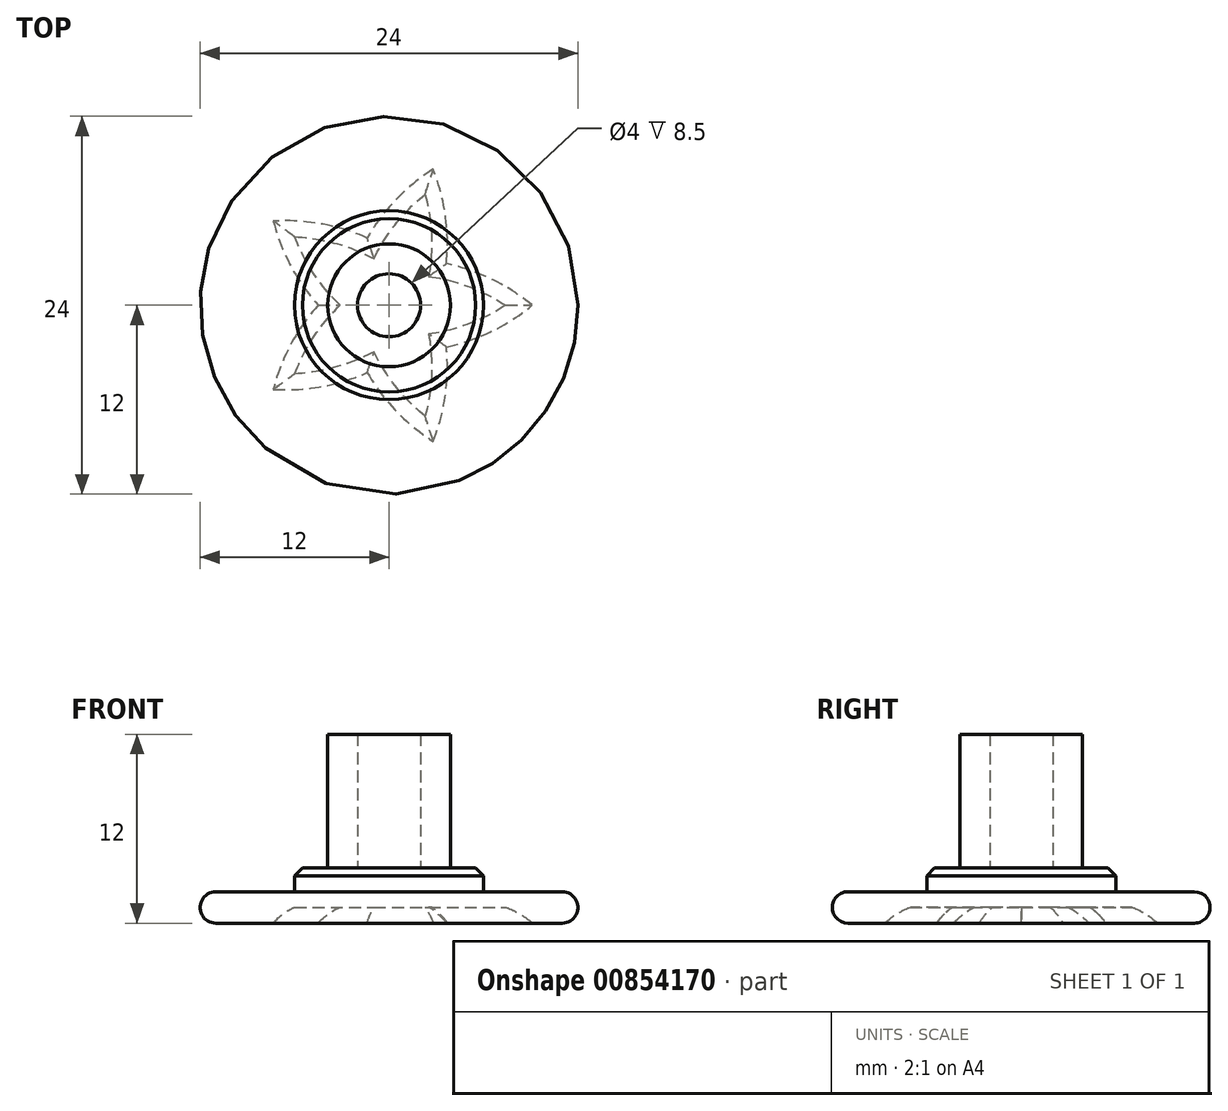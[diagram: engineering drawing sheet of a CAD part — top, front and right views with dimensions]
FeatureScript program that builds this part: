
annotation { "Feature Type Name" : "Feature", "Feature Type Description" : "" }
export const myFeature = defineFeature(function(context is Context, id is Id, definition is map)
    precondition{}
    {
        {
            var Q0;
            Q0=qCreatedBy(makeId("Top.planeOp"),FACE);
            var sketch = newSketch(context, id + "F0", { "sketchPlane" : qUnion([Q0])});
            skCircle(sketch, "E0", {"center": v(0, 0) * mm, "radius": 3.9 * mm});
            skCircle(sketch, "E1", {"center": v(0, 0) * mm, "radius": 2 * mm});
            skCircle(sketch, "E2", {"center": v(0, 0) * mm, "radius": 12 * mm});
            skCircle(sketch, "E3", {"center": v(0, 0) * mm, "radius": 6 * mm});
            skCircle(sketch, "E4.cCircle", {"center": v(0, 0) * mm, "radius": 2.5 * mm, "construction": true});
            skLineSegment(sketch, "E4.0", {"start": v(-2.5, -1.82) * mm, "end": v(-2.5, 1.82) * mm});
            skLineSegment(sketch, "E4.1", {"start": v(-2.5, 1.82) * mm, "end": v(0.95, 2.94) * mm});
            skLineSegment(sketch, "E4.2", {"start": v(0.95, 2.94) * mm, "end": v(3.1, 0) * mm});
            skLineSegment(sketch, "E4.3", {"start": v(3.1, 0) * mm, "end": v(0.95, -2.94) * mm});
            skLineSegment(sketch, "E4.4", {"start": v(0.95, -2.94) * mm, "end": v(-2.5, -1.82) * mm});
            skPoint(sketch, "E4.0.midPoint", {"position": v(-2.5, 0) * mm});
            skLineSegment(sketch, "E5", {"start": v(-2.5, 0) * mm, "end": v(-4.5, 0) * mm});
            skLineSegment(sketch, "E6", {"start": v(-0.77, -2.38) * mm, "end": v(-1.4, -4.28) * mm});
            skLineSegment(sketch, "E7", {"start": v(2.02, -1.47) * mm, "end": v(3.64, -2.65) * mm});
            skLineSegment(sketch, "E8", {"start": v(2.02, 1.47) * mm, "end": v(3.64, 2.65) * mm});
            skLineSegment(sketch, "E9", {"start": v(-0.77, 2.38) * mm, "end": v(-1.4, 4.28) * mm});
            skLineSegment(sketch, "E10", {"start": v(3.1, 0) * mm, "end": v(9.1, 0) * mm});
            skLineSegment(sketch, "E11", {"start": v(0.95, -2.94) * mm, "end": v(2.8, -8.65) * mm});
            skLineSegment(sketch, "E12", {"start": v(-2.5, -1.82) * mm, "end": v(-7.35, -5.34) * mm});
            skLineSegment(sketch, "E13", {"start": v(-2.5, 1.82) * mm, "end": v(-7.35, 5.34) * mm});
            skLineSegment(sketch, "E14", {"start": v(0.95, 2.94) * mm, "end": v(2.8, 8.65) * mm});
            skArc(sketch, "E15", {"start": v(0.95, 2.94) * mm, "mid": v(-3, 4.86) * mm, "end": v(-7.35, 5.34) * mm});
            skArc(sketch, "E16", {"start": v(2.8, 8.65) * mm, "mid": v(-0.44, 5.7) * mm, "end": v(-2.5, 1.82) * mm});
            skArc(sketch, "E17", {"start": v(3.1, 0) * mm, "mid": v(3.7, 4.35) * mm, "end": v(2.8, 8.65) * mm});
            skArc(sketch, "E18", {"start": v(9.1, 0) * mm, "mid": v(5.28, 2.17) * mm, "end": v(0.95, 2.94) * mm});
            skArc(sketch, "E19", {"start": v(0.95, -2.94) * mm, "mid": v(5.28, -2.17) * mm, "end": v(9.1, 0) * mm});
            skArc(sketch, "E20", {"start": v(2.8, -8.65) * mm, "mid": v(3.7, -4.35) * mm, "end": v(3.1, 0) * mm});
            skArc(sketch, "E21", {"start": v(-2.5, -1.82) * mm, "mid": v(-0.44, -5.7) * mm, "end": v(2.8, -8.65) * mm});
            skArc(sketch, "E22", {"start": v(-7.35, -5.34) * mm, "mid": v(-3, -4.86) * mm, "end": v(0.95, -2.94) * mm});
            skArc(sketch, "E23", {"start": v(-2.5, 1.82) * mm, "mid": v(-5.55, -1.34) * mm, "end": v(-7.35, -5.34) * mm});
            skArc(sketch, "E24", {"start": v(-7.35, 5.34) * mm, "mid": v(-5.55, 1.34) * mm, "end": v(-2.5, -1.82) * mm});
            skSolve(sketch);
        }
        {
            var Q0;
            Q0=makeQuery(id+"F0.imprint","IMPRINT",FACE,{"disambiguationData":[TD([[makeQuery(id+"F0.imprint","IMPRINT",EDGE,{"derivedFrom":sQuery(id+"F0.wireOp",EDGE,"E2")}),1.0]])]});
            extrude(context, id + "F1", {"entities" : qUnion([Q0]), "depth" : 2 * mm, "offsetDistance" : 25 * mm});
        }
        {
            var Q0;
            {var subQ0=sQuery(id+"F0.wireOp",EDGE,"E15");var subQ1=sQuery(id+"F0.wireOp",EDGE,"E3");var subQ2=makeQuery(id+"F0.imprint","INTERSECT",VERTEX,{"derivedFrom":[subQ1,subQ0]});Q0=makeQuery(id+"F0.imprint","IMPRINT",FACE,{"disambiguationData":[TD([[makeQuery(id+"F0.imprint","IMPRINT",EDGE,{"disambiguationData":[TD([[subQ2,-1.0]])],"derivedFrom":subQ1}),-1.0]])]});}
            var Q1;
            {var subQ0=sQuery(id+"F0.wireOp",EDGE,"E13");var subQ1=sQuery(id+"F0.wireOp",EDGE,"E3");var subQ2=makeQuery(id+"F0.imprint","INTERSECT",VERTEX,{"derivedFrom":[subQ1,subQ0]});Q1=makeQuery(id+"F0.imprint","IMPRINT",FACE,{"disambiguationData":[TD([[makeQuery(id+"F0.imprint","IMPRINT",EDGE,{"disambiguationData":[TD([[subQ2,-1.0]])],"derivedFrom":subQ1}),-1.0]])]});}
            var Q2;
            {var subQ3=sQuery(id+"F0.wireOp",EDGE,"E0");var subQ5=sQuery(id+"F0.wireOp",EDGE,"E13");var subQ9=makeQuery(id+"F0.imprint","INTERSECT",VERTEX,{"derivedFrom":[subQ3,subQ5]});Q2=makeQuery(id+"F0.imprint","IMPRINT",FACE,{"disambiguationData":[TD([[makeQuery(id+"F0.imprint","IMPRINT",EDGE,{"disambiguationData":[TD([[subQ9,-1.0]])],"derivedFrom":subQ3}),-1.0]])]});}
            var Q3;
            {var subQ0=sQuery(id+"F0.wireOp",EDGE,"E16");var subQ6=sQuery(id+"F0.wireOp",EDGE,"E0");var subQ9=makeQuery(id+"F0.imprint","INTERSECT",VERTEX,{"derivedFrom":[subQ6,subQ0]});Q3=makeQuery(id+"F0.imprint","IMPRINT",FACE,{"disambiguationData":[TD([[makeQuery(id+"F0.imprint","IMPRINT",EDGE,{"disambiguationData":[TD([[subQ9,-1.0]])],"derivedFrom":subQ6}),-1.0]])]});}
            var Q4;
            {var subQ3=sQuery(id+"F0.wireOp",EDGE,"E0");var subQ5=sQuery(id+"F0.wireOp",EDGE,"E14");var subQ6=makeQuery(id+"F0.imprint","INTERSECT",VERTEX,{"derivedFrom":[subQ3,subQ5]});Q4=makeQuery(id+"F0.imprint","IMPRINT",FACE,{"disambiguationData":[TD([[makeQuery(id+"F0.imprint","IMPRINT",EDGE,{"disambiguationData":[TD([[subQ6,-1.0]])],"derivedFrom":subQ3}),-1.0]])]});}
            var Q5;
            {var subQ0=sQuery(id+"F0.wireOp",EDGE,"E14");var subQ1=sQuery(id+"F0.wireOp",EDGE,"E3");var subQ2=makeQuery(id+"F0.imprint","INTERSECT",VERTEX,{"derivedFrom":[subQ1,subQ0]});Q5=makeQuery(id+"F0.imprint","IMPRINT",FACE,{"disambiguationData":[TD([[makeQuery(id+"F0.imprint","IMPRINT",EDGE,{"disambiguationData":[TD([[subQ2,-1.0]])],"derivedFrom":subQ1}),-1.0]])]});}
            var Q6;
            {var subQ0=sQuery(id+"F0.wireOp",EDGE,"E17");var subQ1=sQuery(id+"F0.wireOp",EDGE,"E3");var subQ2=makeQuery(id+"F0.imprint","INTERSECT",VERTEX,{"derivedFrom":[subQ1,subQ0]});Q6=makeQuery(id+"F0.imprint","IMPRINT",FACE,{"disambiguationData":[TD([[makeQuery(id+"F0.imprint","IMPRINT",EDGE,{"disambiguationData":[TD([[subQ2,-1.0]])],"derivedFrom":subQ1}),-1.0]])]});}
            var Q7;
            {var subQ0=sQuery(id+"F0.wireOp",EDGE,"E18");var subQ6=sQuery(id+"F0.wireOp",EDGE,"E0");var subQ9=makeQuery(id+"F0.imprint","INTERSECT",VERTEX,{"derivedFrom":[subQ6,subQ0]});Q7=makeQuery(id+"F0.imprint","IMPRINT",FACE,{"disambiguationData":[TD([[makeQuery(id+"F0.imprint","IMPRINT",EDGE,{"disambiguationData":[TD([[subQ9,-1.0]])],"derivedFrom":subQ6}),-1.0]])]});}
            var Q8;
            {var subQ0=sQuery(id+"F0.wireOp",EDGE,"E15");var subQ1=sQuery(id+"F0.wireOp",EDGE,"E0");var subQ2=makeQuery(id+"F0.imprint","INTERSECT",VERTEX,{"derivedFrom":[subQ1,subQ0]});Q8=makeQuery(id+"F0.imprint","IMPRINT",FACE,{"disambiguationData":[TD([[makeQuery(id+"F0.imprint","IMPRINT",EDGE,{"disambiguationData":[TD([[subQ2,-1.0]])],"derivedFrom":subQ1}),-1.0]])]});}
            var Q9;
            {var subQ0=sQuery(id+"F0.wireOp",EDGE,"E9");var subQ1=sQuery(id+"F0.wireOp",EDGE,"E0");var subQ2=makeQuery(id+"F0.imprint","INTERSECT",VERTEX,{"derivedFrom":[subQ1,subQ0]});Q9=makeQuery(id+"F0.imprint","IMPRINT",FACE,{"disambiguationData":[TD([[makeQuery(id+"F0.imprint","IMPRINT",EDGE,{"disambiguationData":[TD([[subQ2,-1.0]])],"derivedFrom":subQ1}),-1.0]])]});}
            var Q10;
            {var subQ0=sQuery(id+"F0.wireOp",EDGE,"E15");var subQ1=sQuery(id+"F0.wireOp",EDGE,"E0");var subQ2=makeQuery(id+"F0.imprint","INTERSECT",VERTEX,{"derivedFrom":[subQ1,subQ0]});Q10=makeQuery(id+"F0.imprint","IMPRINT",FACE,{"disambiguationData":[TD([[makeQuery(id+"F0.imprint","IMPRINT",EDGE,{"disambiguationData":[TD([[subQ2,-1.0]])],"derivedFrom":subQ1}),1.0]])]});}
            var Q11;
            {var subQ0=sQuery(id+"F0.wireOp",EDGE,"E9");var subQ1=sQuery(id+"F0.wireOp",EDGE,"E0");var subQ2=makeQuery(id+"F0.imprint","INTERSECT",VERTEX,{"derivedFrom":[subQ1,subQ0]});Q11=makeQuery(id+"F0.imprint","IMPRINT",FACE,{"disambiguationData":[TD([[makeQuery(id+"F0.imprint","IMPRINT",EDGE,{"disambiguationData":[TD([[subQ2,-1.0]])],"derivedFrom":subQ1}),1.0]])]});}
            var Q12;
            {var subQ0=sQuery(id+"F0.wireOp",EDGE,"E21");var subQ1=sQuery(id+"F0.wireOp",EDGE,"E3");var subQ2=makeQuery(id+"F0.imprint","INTERSECT",VERTEX,{"derivedFrom":[subQ1,subQ0]});Q12=makeQuery(id+"F0.imprint","IMPRINT",FACE,{"disambiguationData":[TD([[makeQuery(id+"F0.imprint","IMPRINT",EDGE,{"disambiguationData":[TD([[subQ2,-1.0]])],"derivedFrom":subQ1}),-1.0]])]});}
            var Q13;
            {var subQ0=sQuery(id+"F0.wireOp",EDGE,"E11");var subQ1=sQuery(id+"F0.wireOp",EDGE,"E3");var subQ2=makeQuery(id+"F0.imprint","INTERSECT",VERTEX,{"derivedFrom":[subQ1,subQ0]});Q13=makeQuery(id+"F0.imprint","IMPRINT",FACE,{"disambiguationData":[TD([[makeQuery(id+"F0.imprint","IMPRINT",EDGE,{"disambiguationData":[TD([[subQ2,-1.0]])],"derivedFrom":subQ1}),-1.0]])]});}
            var Q14;
            {var subQ0=sQuery(id+"F0.wireOp",EDGE,"E10");var subQ1=sQuery(id+"F0.wireOp",EDGE,"E3");var subQ2=makeQuery(id+"F0.imprint","INTERSECT",VERTEX,{"derivedFrom":[subQ1,subQ0]});Q14=makeQuery(id+"F0.imprint","IMPRINT",FACE,{"disambiguationData":[TD([[makeQuery(id+"F0.imprint","IMPRINT",EDGE,{"disambiguationData":[TD([[subQ2,1.0]])],"derivedFrom":subQ1}),-1.0]])]});}
            var Q15;
            {var subQ0=sQuery(id+"F0.wireOp",EDGE,"E18");var subQ1=sQuery(id+"F0.wireOp",EDGE,"E3");var subQ2=makeQuery(id+"F0.imprint","INTERSECT",VERTEX,{"derivedFrom":[subQ1,subQ0]});Q15=makeQuery(id+"F0.imprint","IMPRINT",FACE,{"disambiguationData":[TD([[makeQuery(id+"F0.imprint","IMPRINT",EDGE,{"disambiguationData":[TD([[subQ2,1.0]])],"derivedFrom":subQ1}),-1.0]])]});}
            var Q16;
            {var subQ0=sQuery(id+"F0.wireOp",EDGE,"E12");var subQ1=sQuery(id+"F0.wireOp",EDGE,"E3");var subQ2=makeQuery(id+"F0.imprint","INTERSECT",VERTEX,{"derivedFrom":[subQ1,subQ0]});Q16=makeQuery(id+"F0.imprint","IMPRINT",FACE,{"disambiguationData":[TD([[makeQuery(id+"F0.imprint","IMPRINT",EDGE,{"disambiguationData":[TD([[subQ2,-1.0]])],"derivedFrom":subQ1}),-1.0]])]});}
            var Q17;
            {var subQ0=sQuery(id+"F0.wireOp",EDGE,"E23");var subQ1=sQuery(id+"F0.wireOp",EDGE,"E3");var subQ2=makeQuery(id+"F0.imprint","INTERSECT",VERTEX,{"derivedFrom":[subQ1,subQ0]});Q17=makeQuery(id+"F0.imprint","IMPRINT",FACE,{"disambiguationData":[TD([[makeQuery(id+"F0.imprint","IMPRINT",EDGE,{"disambiguationData":[TD([[subQ2,-1.0]])],"derivedFrom":subQ1}),-1.0]])]});}
            var Q18;
            {var subQ1=sQuery(id+"F0.wireOp",EDGE,"E0");var subQ7=sQuery(id+"F0.wireOp",EDGE,"E24");var subQ9=makeQuery(id+"F0.imprint","INTERSECT",VERTEX,{"derivedFrom":[subQ1,subQ7]});Q18=makeQuery(id+"F0.imprint","IMPRINT",FACE,{"disambiguationData":[TD([[makeQuery(id+"F0.imprint","IMPRINT",EDGE,{"disambiguationData":[TD([[subQ9,-1.0]])],"derivedFrom":subQ1}),-1.0]])]});}
            var Q19;
            {var subQ0=sQuery(id+"F0.wireOp",EDGE,"E12");var subQ1=sQuery(id+"F0.wireOp",EDGE,"E0");var subQ2=makeQuery(id+"F0.imprint","INTERSECT",VERTEX,{"derivedFrom":[subQ1,subQ0]});Q19=makeQuery(id+"F0.imprint","IMPRINT",FACE,{"disambiguationData":[TD([[makeQuery(id+"F0.imprint","IMPRINT",EDGE,{"disambiguationData":[TD([[subQ2,-1.0]])],"derivedFrom":subQ1}),-1.0]])]});}
            var Q20;
            {var subQ1=sQuery(id+"F0.wireOp",EDGE,"E0");var subQ5=sQuery(id+"F0.wireOp",EDGE,"E22");var subQ9=makeQuery(id+"F0.imprint","INTERSECT",VERTEX,{"derivedFrom":[subQ1,subQ5]});Q20=makeQuery(id+"F0.imprint","IMPRINT",FACE,{"disambiguationData":[TD([[makeQuery(id+"F0.imprint","IMPRINT",EDGE,{"disambiguationData":[TD([[subQ9,-1.0]])],"derivedFrom":subQ1}),-1.0]])]});}
            var Q21;
            {var subQ3=sQuery(id+"F0.wireOp",EDGE,"E0");var subQ5=sQuery(id+"F0.wireOp",EDGE,"E11");var subQ9=makeQuery(id+"F0.imprint","INTERSECT",VERTEX,{"derivedFrom":[subQ3,subQ5]});Q21=makeQuery(id+"F0.imprint","IMPRINT",FACE,{"disambiguationData":[TD([[makeQuery(id+"F0.imprint","IMPRINT",EDGE,{"disambiguationData":[TD([[subQ9,-1.0]])],"derivedFrom":subQ3}),-1.0]])]});}
            var Q22;
            {var subQ5=sQuery(id+"F0.wireOp",EDGE,"E10");var subQ6=sQuery(id+"F0.wireOp",EDGE,"E0");var subQ7=makeQuery(id+"F0.imprint","INTERSECT",VERTEX,{"derivedFrom":[subQ6,subQ5]});Q22=makeQuery(id+"F0.imprint","IMPRINT",FACE,{"disambiguationData":[TD([[makeQuery(id+"F0.imprint","IMPRINT",EDGE,{"disambiguationData":[TD([[subQ7,1.0]])],"derivedFrom":subQ6}),-1.0]])]});}
            var Q23;
            {var subQ1=sQuery(id+"F0.wireOp",EDGE,"E17");var subQ3=sQuery(id+"F0.wireOp",EDGE,"E0");var subQ4=makeQuery(id+"F0.imprint","INTERSECT",VERTEX,{"derivedFrom":[subQ3,subQ1]});Q23=makeQuery(id+"F0.imprint","IMPRINT",FACE,{"disambiguationData":[TD([[makeQuery(id+"F0.imprint","IMPRINT",EDGE,{"disambiguationData":[TD([[subQ4,1.0]])],"derivedFrom":subQ3}),-1.0]])]});}
            var Q24;
            {var subQ0=sQuery(id+"F0.wireOp",EDGE,"E8");var subQ1=sQuery(id+"F0.wireOp",EDGE,"E0");var subQ2=makeQuery(id+"F0.imprint","INTERSECT",VERTEX,{"derivedFrom":[subQ1,subQ0]});Q24=makeQuery(id+"F0.imprint","IMPRINT",FACE,{"disambiguationData":[TD([[makeQuery(id+"F0.imprint","IMPRINT",EDGE,{"disambiguationData":[TD([[subQ2,-1.0]])],"derivedFrom":subQ1}),1.0]])]});}
            var Q25;
            {var subQ0=sQuery(id+"F0.wireOp",EDGE,"E17");var subQ1=sQuery(id+"F0.wireOp",EDGE,"E0");var subQ2=makeQuery(id+"F0.imprint","INTERSECT",VERTEX,{"derivedFrom":[subQ1,subQ0]});Q25=makeQuery(id+"F0.imprint","IMPRINT",FACE,{"disambiguationData":[TD([[makeQuery(id+"F0.imprint","IMPRINT",EDGE,{"disambiguationData":[TD([[subQ2,-1.0]])],"derivedFrom":subQ1}),1.0]])]});}
            var Q26;
            {var subQ0=sQuery(id+"F0.wireOp",EDGE,"E8");var subQ1=sQuery(id+"F0.wireOp",EDGE,"E0");var subQ2=makeQuery(id+"F0.imprint","INTERSECT",VERTEX,{"derivedFrom":[subQ1,subQ0]});Q26=makeQuery(id+"F0.imprint","IMPRINT",FACE,{"disambiguationData":[TD([[makeQuery(id+"F0.imprint","IMPRINT",EDGE,{"disambiguationData":[TD([[subQ2,-1.0]])],"derivedFrom":subQ1}),-1.0]])]});}
            var Q27;
            {var subQ0=sQuery(id+"F0.wireOp",EDGE,"E17");var subQ1=sQuery(id+"F0.wireOp",EDGE,"E0");var subQ2=makeQuery(id+"F0.imprint","INTERSECT",VERTEX,{"derivedFrom":[subQ1,subQ0]});Q27=makeQuery(id+"F0.imprint","IMPRINT",FACE,{"disambiguationData":[TD([[makeQuery(id+"F0.imprint","IMPRINT",EDGE,{"disambiguationData":[TD([[subQ2,-1.0]])],"derivedFrom":subQ1}),-1.0]])]});}
            var Q28;
            {var subQ0=sQuery(id+"F0.wireOp",EDGE,"E23");var subQ1=sQuery(id+"F0.wireOp",EDGE,"E0");var subQ2=makeQuery(id+"F0.imprint","INTERSECT",VERTEX,{"derivedFrom":[subQ1,subQ0]});Q28=makeQuery(id+"F0.imprint","IMPRINT",FACE,{"disambiguationData":[TD([[makeQuery(id+"F0.imprint","IMPRINT",EDGE,{"disambiguationData":[TD([[subQ2,-1.0]])],"derivedFrom":subQ1}),-1.0]])]});}
            var Q29;
            {var subQ0=sQuery(id+"F0.wireOp",EDGE,"E5");var subQ1=sQuery(id+"F0.wireOp",EDGE,"E0");var subQ2=makeQuery(id+"F0.imprint","INTERSECT",VERTEX,{"derivedFrom":[subQ1,subQ0]});Q29=makeQuery(id+"F0.imprint","IMPRINT",FACE,{"disambiguationData":[TD([[makeQuery(id+"F0.imprint","IMPRINT",EDGE,{"disambiguationData":[TD([[subQ2,-1.0]])],"derivedFrom":subQ1}),-1.0]])]});}
            var Q30;
            {var subQ0=sQuery(id+"F0.wireOp",EDGE,"E21");var subQ1=sQuery(id+"F0.wireOp",EDGE,"E0");var subQ2=makeQuery(id+"F0.imprint","INTERSECT",VERTEX,{"derivedFrom":[subQ1,subQ0]});Q30=makeQuery(id+"F0.imprint","IMPRINT",FACE,{"disambiguationData":[TD([[makeQuery(id+"F0.imprint","IMPRINT",EDGE,{"disambiguationData":[TD([[subQ2,-1.0]])],"derivedFrom":subQ1}),-1.0]])]});}
            var Q31;
            {var subQ0=sQuery(id+"F0.wireOp",EDGE,"E6");var subQ1=sQuery(id+"F0.wireOp",EDGE,"E0");var subQ2=makeQuery(id+"F0.imprint","INTERSECT",VERTEX,{"derivedFrom":[subQ1,subQ0]});Q31=makeQuery(id+"F0.imprint","IMPRINT",FACE,{"disambiguationData":[TD([[makeQuery(id+"F0.imprint","IMPRINT",EDGE,{"disambiguationData":[TD([[subQ2,-1.0]])],"derivedFrom":subQ1}),-1.0]])]});}
            var Q32;
            {var subQ0=sQuery(id+"F0.wireOp",EDGE,"E19");var subQ1=sQuery(id+"F0.wireOp",EDGE,"E0");var subQ2=makeQuery(id+"F0.imprint","INTERSECT",VERTEX,{"derivedFrom":[subQ1,subQ0]});Q32=makeQuery(id+"F0.imprint","IMPRINT",FACE,{"disambiguationData":[TD([[makeQuery(id+"F0.imprint","IMPRINT",EDGE,{"disambiguationData":[TD([[subQ2,-1.0]])],"derivedFrom":subQ1}),-1.0]])]});}
            var Q33;
            {var subQ0=sQuery(id+"F0.wireOp",EDGE,"E7");var subQ1=sQuery(id+"F0.wireOp",EDGE,"E0");var subQ2=makeQuery(id+"F0.imprint","INTERSECT",VERTEX,{"derivedFrom":[subQ1,subQ0]});Q33=makeQuery(id+"F0.imprint","IMPRINT",FACE,{"disambiguationData":[TD([[makeQuery(id+"F0.imprint","IMPRINT",EDGE,{"disambiguationData":[TD([[subQ2,-1.0]])],"derivedFrom":subQ1}),-1.0]])]});}
            var Q34;
            {var subQ0=sQuery(id+"F0.wireOp",EDGE,"E10");var subQ1=sQuery(id+"F0.wireOp",EDGE,"E0");var subQ2=makeQuery(id+"F0.imprint","INTERSECT",VERTEX,{"derivedFrom":[subQ1,subQ0]});Q34=makeQuery(id+"F0.imprint","IMPRINT",FACE,{"disambiguationData":[TD([[makeQuery(id+"F0.imprint","IMPRINT",EDGE,{"disambiguationData":[TD([[subQ2,1.0]])],"derivedFrom":subQ1}),1.0]])]});}
            var Q35;
            {var subQ0=sQuery(id+"F0.wireOp",EDGE,"E17");var subQ1=sQuery(id+"F0.wireOp",EDGE,"E0");var subQ2=makeQuery(id+"F0.imprint","INTERSECT",VERTEX,{"derivedFrom":[subQ1,subQ0]});Q35=makeQuery(id+"F0.imprint","IMPRINT",FACE,{"disambiguationData":[TD([[makeQuery(id+"F0.imprint","IMPRINT",EDGE,{"disambiguationData":[TD([[subQ2,1.0]])],"derivedFrom":subQ1}),1.0]])]});}
            var Q36;
            {var subQ0=sQuery(id+"F0.wireOp",EDGE,"E18");var subQ1=sQuery(id+"F0.wireOp",EDGE,"E0");var subQ2=makeQuery(id+"F0.imprint","INTERSECT",VERTEX,{"derivedFrom":[subQ1,subQ0]});Q36=makeQuery(id+"F0.imprint","IMPRINT",FACE,{"disambiguationData":[TD([[makeQuery(id+"F0.imprint","IMPRINT",EDGE,{"disambiguationData":[TD([[subQ2,-1.0]])],"derivedFrom":subQ1}),1.0]])]});}
            var Q37;
            {var subQ0=sQuery(id+"F0.wireOp",EDGE,"E14");var subQ1=sQuery(id+"F0.wireOp",EDGE,"E0");var subQ2=makeQuery(id+"F0.imprint","INTERSECT",VERTEX,{"derivedFrom":[subQ1,subQ0]});Q37=makeQuery(id+"F0.imprint","IMPRINT",FACE,{"disambiguationData":[TD([[makeQuery(id+"F0.imprint","IMPRINT",EDGE,{"disambiguationData":[TD([[subQ2,-1.0]])],"derivedFrom":subQ1}),1.0]])]});}
            var Q38;
            {var subQ0=sQuery(id+"F0.wireOp",EDGE,"E16");var subQ1=sQuery(id+"F0.wireOp",EDGE,"E0");var subQ2=makeQuery(id+"F0.imprint","INTERSECT",VERTEX,{"derivedFrom":[subQ1,subQ0]});Q38=makeQuery(id+"F0.imprint","IMPRINT",FACE,{"disambiguationData":[TD([[makeQuery(id+"F0.imprint","IMPRINT",EDGE,{"disambiguationData":[TD([[subQ2,-1.0]])],"derivedFrom":subQ1}),1.0]])]});}
            var Q39;
            {var subQ0=sQuery(id+"F0.wireOp",EDGE,"E13");var subQ1=sQuery(id+"F0.wireOp",EDGE,"E0");var subQ2=makeQuery(id+"F0.imprint","INTERSECT",VERTEX,{"derivedFrom":[subQ1,subQ0]});Q39=makeQuery(id+"F0.imprint","IMPRINT",FACE,{"disambiguationData":[TD([[makeQuery(id+"F0.imprint","IMPRINT",EDGE,{"disambiguationData":[TD([[subQ2,-1.0]])],"derivedFrom":subQ1}),1.0]])]});}
            var Q40;
            {var subQ0=sQuery(id+"F0.wireOp",EDGE,"E24");var subQ1=sQuery(id+"F0.wireOp",EDGE,"E0");var subQ2=makeQuery(id+"F0.imprint","INTERSECT",VERTEX,{"derivedFrom":[subQ1,subQ0]});Q40=makeQuery(id+"F0.imprint","IMPRINT",FACE,{"disambiguationData":[TD([[makeQuery(id+"F0.imprint","IMPRINT",EDGE,{"disambiguationData":[TD([[subQ2,-1.0]])],"derivedFrom":subQ1}),1.0]])]});}
            var Q41;
            {var subQ0=sQuery(id+"F0.wireOp",EDGE,"E12");var subQ1=sQuery(id+"F0.wireOp",EDGE,"E0");var subQ2=makeQuery(id+"F0.imprint","INTERSECT",VERTEX,{"derivedFrom":[subQ1,subQ0]});Q41=makeQuery(id+"F0.imprint","IMPRINT",FACE,{"disambiguationData":[TD([[makeQuery(id+"F0.imprint","IMPRINT",EDGE,{"disambiguationData":[TD([[subQ2,-1.0]])],"derivedFrom":subQ1}),1.0]])]});}
            var Q42;
            {var subQ0=sQuery(id+"F0.wireOp",EDGE,"E22");var subQ1=sQuery(id+"F0.wireOp",EDGE,"E0");var subQ2=makeQuery(id+"F0.imprint","INTERSECT",VERTEX,{"derivedFrom":[subQ1,subQ0]});Q42=makeQuery(id+"F0.imprint","IMPRINT",FACE,{"disambiguationData":[TD([[makeQuery(id+"F0.imprint","IMPRINT",EDGE,{"disambiguationData":[TD([[subQ2,-1.0]])],"derivedFrom":subQ1}),1.0]])]});}
            var Q43;
            {var subQ0=sQuery(id+"F0.wireOp",EDGE,"E11");var subQ1=sQuery(id+"F0.wireOp",EDGE,"E0");var subQ2=makeQuery(id+"F0.imprint","INTERSECT",VERTEX,{"derivedFrom":[subQ1,subQ0]});Q43=makeQuery(id+"F0.imprint","IMPRINT",FACE,{"disambiguationData":[TD([[makeQuery(id+"F0.imprint","IMPRINT",EDGE,{"disambiguationData":[TD([[subQ2,-1.0]])],"derivedFrom":subQ1}),1.0]])]});}
            var Q44;
            {var subQ0=sQuery(id+"F0.wireOp",EDGE,"E19");var subQ1=sQuery(id+"F0.wireOp",EDGE,"E0");var subQ2=makeQuery(id+"F0.imprint","INTERSECT",VERTEX,{"derivedFrom":[subQ1,subQ0]});Q44=makeQuery(id+"F0.imprint","IMPRINT",FACE,{"disambiguationData":[TD([[makeQuery(id+"F0.imprint","IMPRINT",EDGE,{"disambiguationData":[TD([[subQ2,-1.0]])],"derivedFrom":subQ1}),1.0]])]});}
            var Q45;
            {var subQ0=sQuery(id+"F0.wireOp",EDGE,"E7");var subQ1=sQuery(id+"F0.wireOp",EDGE,"E0");var subQ2=makeQuery(id+"F0.imprint","INTERSECT",VERTEX,{"derivedFrom":[subQ1,subQ0]});Q45=makeQuery(id+"F0.imprint","IMPRINT",FACE,{"disambiguationData":[TD([[makeQuery(id+"F0.imprint","IMPRINT",EDGE,{"disambiguationData":[TD([[subQ2,-1.0]])],"derivedFrom":subQ1}),1.0]])]});}
            var Q46;
            {var subQ0=sQuery(id+"F0.wireOp",EDGE,"E6");var subQ1=sQuery(id+"F0.wireOp",EDGE,"E0");var subQ2=makeQuery(id+"F0.imprint","INTERSECT",VERTEX,{"derivedFrom":[subQ1,subQ0]});Q46=makeQuery(id+"F0.imprint","IMPRINT",FACE,{"disambiguationData":[TD([[makeQuery(id+"F0.imprint","IMPRINT",EDGE,{"disambiguationData":[TD([[subQ2,-1.0]])],"derivedFrom":subQ1}),1.0]])]});}
            var Q47;
            {var subQ0=sQuery(id+"F0.wireOp",EDGE,"E21");var subQ1=sQuery(id+"F0.wireOp",EDGE,"E0");var subQ2=makeQuery(id+"F0.imprint","INTERSECT",VERTEX,{"derivedFrom":[subQ1,subQ0]});Q47=makeQuery(id+"F0.imprint","IMPRINT",FACE,{"disambiguationData":[TD([[makeQuery(id+"F0.imprint","IMPRINT",EDGE,{"disambiguationData":[TD([[subQ2,-1.0]])],"derivedFrom":subQ1}),1.0]])]});}
            var Q48;
            {var subQ0=sQuery(id+"F0.wireOp",EDGE,"E5");var subQ1=sQuery(id+"F0.wireOp",EDGE,"E0");var subQ2=makeQuery(id+"F0.imprint","INTERSECT",VERTEX,{"derivedFrom":[subQ1,subQ0]});Q48=makeQuery(id+"F0.imprint","IMPRINT",FACE,{"disambiguationData":[TD([[makeQuery(id+"F0.imprint","IMPRINT",EDGE,{"disambiguationData":[TD([[subQ2,-1.0]])],"derivedFrom":subQ1}),1.0]])]});}
            var Q49;
            {var subQ0=sQuery(id+"F0.wireOp",EDGE,"E23");var subQ1=sQuery(id+"F0.wireOp",EDGE,"E0");var subQ2=makeQuery(id+"F0.imprint","INTERSECT",VERTEX,{"derivedFrom":[subQ1,subQ0]});Q49=makeQuery(id+"F0.imprint","IMPRINT",FACE,{"disambiguationData":[TD([[makeQuery(id+"F0.imprint","IMPRINT",EDGE,{"disambiguationData":[TD([[subQ2,-1.0]])],"derivedFrom":subQ1}),1.0]])]});}
            var Q50;
            Q50=makeQuery(id+"F0.imprint","IMPRINT",FACE,{"disambiguationData":[TD([[makeQuery(id+"F0.imprint","IMPRINT",EDGE,{"derivedFrom":sQuery(id+"F0.wireOp",EDGE,"E1")}),-1.0]])]});
            var Q51;
            Q51=makeQuery(id+"F0.imprint","IMPRINT",FACE,{"disambiguationData":[TD([[makeQuery(id+"F0.imprint","IMPRINT",EDGE,{"derivedFrom":sQuery(id+"F0.wireOp",EDGE,"E1")}),1.0]])]});
            extrude(context, id + "F2", {"entities" : qUnion([Q0, Q1, Q2, Q3, Q4, Q5, Q6, Q7, Q8, Q9, Q10, Q11, Q12, Q13, Q14, Q15, Q16, Q17, Q18, Q19, Q20, Q21, Q22, Q23, Q24, Q25, Q26, Q27, Q28, Q29, Q30, Q31, Q32, Q33, Q34, Q35, Q36, Q37, Q38, Q39, Q40, Q41, Q42, Q43, Q44, Q45, Q46, Q47, Q48, Q49, Q50, Q51]), "operationType" : NewBodyOperationType.ADD, "depth" : 2 * mm, "offsetDistance" : 25 * mm, "hasSecondDirection" : true, "secondDirectionOppositeDirection" : false, "secondDirectionDepth" : 1 * mm});
        }
        {
            var Q0;
            {var subQ0=sQuery(id+"F0.wireOp",EDGE,"E24");var subQ1=sQuery(id+"F0.wireOp",EDGE,"E3");var subQ2=makeQuery(id+"F0.imprint","INTERSECT",VERTEX,{"derivedFrom":[subQ1,subQ0]});Q0=makeQuery(id+"F0.imprint","IMPRINT",FACE,{"disambiguationData":[TD([[makeQuery(id+"F0.imprint","IMPRINT",EDGE,{"disambiguationData":[TD([[subQ2,-1.0]])],"derivedFrom":subQ1}),1.0]])]});}
            var Q1;
            {var subQ0=sQuery(id+"F0.wireOp",EDGE,"E16");var subQ1=sQuery(id+"F0.wireOp",EDGE,"E3");var subQ2=makeQuery(id+"F0.imprint","INTERSECT",VERTEX,{"derivedFrom":[subQ1,subQ0]});Q1=makeQuery(id+"F0.imprint","IMPRINT",FACE,{"disambiguationData":[TD([[makeQuery(id+"F0.imprint","IMPRINT",EDGE,{"disambiguationData":[TD([[subQ2,-1.0]])],"derivedFrom":subQ1}),1.0]])]});}
            var Q2;
            {var subQ0=sQuery(id+"F0.wireOp",EDGE,"E18");var subQ1=sQuery(id+"F0.wireOp",EDGE,"E3");var subQ2=makeQuery(id+"F0.imprint","INTERSECT",VERTEX,{"derivedFrom":[subQ1,subQ0]});Q2=makeQuery(id+"F0.imprint","IMPRINT",FACE,{"disambiguationData":[TD([[makeQuery(id+"F0.imprint","IMPRINT",EDGE,{"disambiguationData":[TD([[subQ2,-1.0]])],"derivedFrom":subQ1}),1.0]])]});}
            var Q3;
            {var subQ0=sQuery(id+"F0.wireOp",EDGE,"E20");var subQ1=sQuery(id+"F0.wireOp",EDGE,"E3");var subQ2=makeQuery(id+"F0.imprint","INTERSECT",VERTEX,{"derivedFrom":[subQ1,subQ0]});Q3=makeQuery(id+"F0.imprint","IMPRINT",FACE,{"disambiguationData":[TD([[makeQuery(id+"F0.imprint","IMPRINT",EDGE,{"disambiguationData":[TD([[subQ2,-1.0]])],"derivedFrom":subQ1}),1.0]])]});}
            var Q4;
            {var subQ0=sQuery(id+"F0.wireOp",EDGE,"E22");var subQ1=sQuery(id+"F0.wireOp",EDGE,"E3");var subQ2=makeQuery(id+"F0.imprint","INTERSECT",VERTEX,{"derivedFrom":[subQ1,subQ0]});Q4=makeQuery(id+"F0.imprint","IMPRINT",FACE,{"disambiguationData":[TD([[makeQuery(id+"F0.imprint","IMPRINT",EDGE,{"disambiguationData":[TD([[subQ2,-1.0]])],"derivedFrom":subQ1}),1.0]])]});}
            extrude(context, id + "F3", {"entities" : qUnion([Q0, Q1, Q2, Q3, Q4]), "operationType" : NewBodyOperationType.ADD, "depth" : 3.5 * mm, "offsetDistance" : 25 * mm});
        }
        {
            var Q0;
            {var subQ0=sQuery(id+"F0.wireOp",EDGE,"E12");var subQ1=sQuery(id+"F0.wireOp",EDGE,"E0");var subQ2=makeQuery(id+"F0.imprint","INTERSECT",VERTEX,{"derivedFrom":[subQ1,subQ0]});Q0=makeQuery(id+"F0.imprint","IMPRINT",FACE,{"disambiguationData":[TD([[makeQuery(id+"F0.imprint","IMPRINT",EDGE,{"disambiguationData":[TD([[subQ2,-1.0]])],"derivedFrom":subQ1}),-1.0]])]});}
            var Q1;
            {var subQ1=sQuery(id+"F0.wireOp",EDGE,"E0");var subQ7=sQuery(id+"F0.wireOp",EDGE,"E24");var subQ9=makeQuery(id+"F0.imprint","INTERSECT",VERTEX,{"derivedFrom":[subQ1,subQ7]});Q1=makeQuery(id+"F0.imprint","IMPRINT",FACE,{"disambiguationData":[TD([[makeQuery(id+"F0.imprint","IMPRINT",EDGE,{"disambiguationData":[TD([[subQ9,-1.0]])],"derivedFrom":subQ1}),-1.0]])]});}
            var Q2;
            {var subQ1=sQuery(id+"F0.wireOp",EDGE,"E0");var subQ5=sQuery(id+"F0.wireOp",EDGE,"E22");var subQ9=makeQuery(id+"F0.imprint","INTERSECT",VERTEX,{"derivedFrom":[subQ1,subQ5]});Q2=makeQuery(id+"F0.imprint","IMPRINT",FACE,{"disambiguationData":[TD([[makeQuery(id+"F0.imprint","IMPRINT",EDGE,{"disambiguationData":[TD([[subQ9,-1.0]])],"derivedFrom":subQ1}),-1.0]])]});}
            var Q3;
            {var subQ3=sQuery(id+"F0.wireOp",EDGE,"E0");var subQ5=sQuery(id+"F0.wireOp",EDGE,"E11");var subQ9=makeQuery(id+"F0.imprint","INTERSECT",VERTEX,{"derivedFrom":[subQ3,subQ5]});Q3=makeQuery(id+"F0.imprint","IMPRINT",FACE,{"disambiguationData":[TD([[makeQuery(id+"F0.imprint","IMPRINT",EDGE,{"disambiguationData":[TD([[subQ9,-1.0]])],"derivedFrom":subQ3}),-1.0]])]});}
            var Q4;
            {var subQ0=sQuery(id+"F0.wireOp",EDGE,"E6");var subQ1=sQuery(id+"F0.wireOp",EDGE,"E0");var subQ2=makeQuery(id+"F0.imprint","INTERSECT",VERTEX,{"derivedFrom":[subQ1,subQ0]});Q4=makeQuery(id+"F0.imprint","IMPRINT",FACE,{"disambiguationData":[TD([[makeQuery(id+"F0.imprint","IMPRINT",EDGE,{"disambiguationData":[TD([[subQ2,-1.0]])],"derivedFrom":subQ1}),-1.0]])]});}
            var Q5;
            {var subQ0=sQuery(id+"F0.wireOp",EDGE,"E21");var subQ1=sQuery(id+"F0.wireOp",EDGE,"E0");var subQ2=makeQuery(id+"F0.imprint","INTERSECT",VERTEX,{"derivedFrom":[subQ1,subQ0]});Q5=makeQuery(id+"F0.imprint","IMPRINT",FACE,{"disambiguationData":[TD([[makeQuery(id+"F0.imprint","IMPRINT",EDGE,{"disambiguationData":[TD([[subQ2,-1.0]])],"derivedFrom":subQ1}),-1.0]])]});}
            var Q6;
            {var subQ0=sQuery(id+"F0.wireOp",EDGE,"E19");var subQ1=sQuery(id+"F0.wireOp",EDGE,"E0");var subQ2=makeQuery(id+"F0.imprint","INTERSECT",VERTEX,{"derivedFrom":[subQ1,subQ0]});Q6=makeQuery(id+"F0.imprint","IMPRINT",FACE,{"disambiguationData":[TD([[makeQuery(id+"F0.imprint","IMPRINT",EDGE,{"disambiguationData":[TD([[subQ2,-1.0]])],"derivedFrom":subQ1}),-1.0]])]});}
            var Q7;
            {var subQ0=sQuery(id+"F0.wireOp",EDGE,"E7");var subQ1=sQuery(id+"F0.wireOp",EDGE,"E0");var subQ2=makeQuery(id+"F0.imprint","INTERSECT",VERTEX,{"derivedFrom":[subQ1,subQ0]});Q7=makeQuery(id+"F0.imprint","IMPRINT",FACE,{"disambiguationData":[TD([[makeQuery(id+"F0.imprint","IMPRINT",EDGE,{"disambiguationData":[TD([[subQ2,-1.0]])],"derivedFrom":subQ1}),-1.0]])]});}
            var Q8;
            {var subQ5=sQuery(id+"F0.wireOp",EDGE,"E10");var subQ6=sQuery(id+"F0.wireOp",EDGE,"E0");var subQ7=makeQuery(id+"F0.imprint","INTERSECT",VERTEX,{"derivedFrom":[subQ6,subQ5]});Q8=makeQuery(id+"F0.imprint","IMPRINT",FACE,{"disambiguationData":[TD([[makeQuery(id+"F0.imprint","IMPRINT",EDGE,{"disambiguationData":[TD([[subQ7,1.0]])],"derivedFrom":subQ6}),-1.0]])]});}
            var Q9;
            {var subQ1=sQuery(id+"F0.wireOp",EDGE,"E17");var subQ3=sQuery(id+"F0.wireOp",EDGE,"E0");var subQ4=makeQuery(id+"F0.imprint","INTERSECT",VERTEX,{"derivedFrom":[subQ3,subQ1]});Q9=makeQuery(id+"F0.imprint","IMPRINT",FACE,{"disambiguationData":[TD([[makeQuery(id+"F0.imprint","IMPRINT",EDGE,{"disambiguationData":[TD([[subQ4,1.0]])],"derivedFrom":subQ3}),-1.0]])]});}
            var Q10;
            {var subQ0=sQuery(id+"F0.wireOp",EDGE,"E17");var subQ1=sQuery(id+"F0.wireOp",EDGE,"E0");var subQ2=makeQuery(id+"F0.imprint","INTERSECT",VERTEX,{"derivedFrom":[subQ1,subQ0]});Q10=makeQuery(id+"F0.imprint","IMPRINT",FACE,{"disambiguationData":[TD([[makeQuery(id+"F0.imprint","IMPRINT",EDGE,{"disambiguationData":[TD([[subQ2,-1.0]])],"derivedFrom":subQ1}),-1.0]])]});}
            var Q11;
            {var subQ0=sQuery(id+"F0.wireOp",EDGE,"E8");var subQ1=sQuery(id+"F0.wireOp",EDGE,"E0");var subQ2=makeQuery(id+"F0.imprint","INTERSECT",VERTEX,{"derivedFrom":[subQ1,subQ0]});Q11=makeQuery(id+"F0.imprint","IMPRINT",FACE,{"disambiguationData":[TD([[makeQuery(id+"F0.imprint","IMPRINT",EDGE,{"disambiguationData":[TD([[subQ2,-1.0]])],"derivedFrom":subQ1}),-1.0]])]});}
            var Q12;
            {var subQ0=sQuery(id+"F0.wireOp",EDGE,"E18");var subQ6=sQuery(id+"F0.wireOp",EDGE,"E0");var subQ9=makeQuery(id+"F0.imprint","INTERSECT",VERTEX,{"derivedFrom":[subQ6,subQ0]});Q12=makeQuery(id+"F0.imprint","IMPRINT",FACE,{"disambiguationData":[TD([[makeQuery(id+"F0.imprint","IMPRINT",EDGE,{"disambiguationData":[TD([[subQ9,-1.0]])],"derivedFrom":subQ6}),-1.0]])]});}
            var Q13;
            {var subQ3=sQuery(id+"F0.wireOp",EDGE,"E0");var subQ5=sQuery(id+"F0.wireOp",EDGE,"E14");var subQ6=makeQuery(id+"F0.imprint","INTERSECT",VERTEX,{"derivedFrom":[subQ3,subQ5]});Q13=makeQuery(id+"F0.imprint","IMPRINT",FACE,{"disambiguationData":[TD([[makeQuery(id+"F0.imprint","IMPRINT",EDGE,{"disambiguationData":[TD([[subQ6,-1.0]])],"derivedFrom":subQ3}),-1.0]])]});}
            var Q14;
            {var subQ0=sQuery(id+"F0.wireOp",EDGE,"E15");var subQ1=sQuery(id+"F0.wireOp",EDGE,"E0");var subQ2=makeQuery(id+"F0.imprint","INTERSECT",VERTEX,{"derivedFrom":[subQ1,subQ0]});Q14=makeQuery(id+"F0.imprint","IMPRINT",FACE,{"disambiguationData":[TD([[makeQuery(id+"F0.imprint","IMPRINT",EDGE,{"disambiguationData":[TD([[subQ2,-1.0]])],"derivedFrom":subQ1}),-1.0]])]});}
            var Q15;
            {var subQ0=sQuery(id+"F0.wireOp",EDGE,"E9");var subQ1=sQuery(id+"F0.wireOp",EDGE,"E0");var subQ2=makeQuery(id+"F0.imprint","INTERSECT",VERTEX,{"derivedFrom":[subQ1,subQ0]});Q15=makeQuery(id+"F0.imprint","IMPRINT",FACE,{"disambiguationData":[TD([[makeQuery(id+"F0.imprint","IMPRINT",EDGE,{"disambiguationData":[TD([[subQ2,-1.0]])],"derivedFrom":subQ1}),-1.0]])]});}
            var Q16;
            {var subQ0=sQuery(id+"F0.wireOp",EDGE,"E16");var subQ6=sQuery(id+"F0.wireOp",EDGE,"E0");var subQ9=makeQuery(id+"F0.imprint","INTERSECT",VERTEX,{"derivedFrom":[subQ6,subQ0]});Q16=makeQuery(id+"F0.imprint","IMPRINT",FACE,{"disambiguationData":[TD([[makeQuery(id+"F0.imprint","IMPRINT",EDGE,{"disambiguationData":[TD([[subQ9,-1.0]])],"derivedFrom":subQ6}),-1.0]])]});}
            var Q17;
            {var subQ3=sQuery(id+"F0.wireOp",EDGE,"E0");var subQ5=sQuery(id+"F0.wireOp",EDGE,"E13");var subQ9=makeQuery(id+"F0.imprint","INTERSECT",VERTEX,{"derivedFrom":[subQ3,subQ5]});Q17=makeQuery(id+"F0.imprint","IMPRINT",FACE,{"disambiguationData":[TD([[makeQuery(id+"F0.imprint","IMPRINT",EDGE,{"disambiguationData":[TD([[subQ9,-1.0]])],"derivedFrom":subQ3}),-1.0]])]});}
            var Q18;
            {var subQ0=sQuery(id+"F0.wireOp",EDGE,"E23");var subQ1=sQuery(id+"F0.wireOp",EDGE,"E0");var subQ2=makeQuery(id+"F0.imprint","INTERSECT",VERTEX,{"derivedFrom":[subQ1,subQ0]});Q18=makeQuery(id+"F0.imprint","IMPRINT",FACE,{"disambiguationData":[TD([[makeQuery(id+"F0.imprint","IMPRINT",EDGE,{"disambiguationData":[TD([[subQ2,-1.0]])],"derivedFrom":subQ1}),-1.0]])]});}
            var Q19;
            {var subQ0=sQuery(id+"F0.wireOp",EDGE,"E5");var subQ1=sQuery(id+"F0.wireOp",EDGE,"E0");var subQ2=makeQuery(id+"F0.imprint","INTERSECT",VERTEX,{"derivedFrom":[subQ1,subQ0]});Q19=makeQuery(id+"F0.imprint","IMPRINT",FACE,{"disambiguationData":[TD([[makeQuery(id+"F0.imprint","IMPRINT",EDGE,{"disambiguationData":[TD([[subQ2,-1.0]])],"derivedFrom":subQ1}),-1.0]])]});}
            var Q20;
            Q20=makeQuery(id+"F0.imprint","IMPRINT",FACE,{"disambiguationData":[TD([[makeQuery(id+"F0.imprint","IMPRINT",EDGE,{"derivedFrom":sQuery(id+"F0.wireOp",EDGE,"E1")}),1.0]])]});
            extrude(context, id + "F4", {"entities" : qUnion([Q0, Q1, Q2, Q3, Q4, Q5, Q6, Q7, Q8, Q9, Q10, Q11, Q12, Q13, Q14, Q15, Q16, Q17, Q18, Q19, Q20]), "operationType" : NewBodyOperationType.ADD, "depth" : 3.5 * mm, "offsetDistance" : 25 * mm, "hasSecondDirection" : true, "secondDirectionOppositeDirection" : false, "secondDirectionDepth" : 1 * mm});
        }
        {
            var Q0;
            Q0=makeQuery(id+"F0.imprint","IMPRINT",FACE,{"disambiguationData":[TD([[makeQuery(id+"F0.imprint","IMPRINT",EDGE,{"derivedFrom":sQuery(id+"F0.wireOp",EDGE,"E1")}),-1.0]])]});
            var Q1;
            {var subQ0=sQuery(id+"F0.wireOp",EDGE,"E21");var subQ1=sQuery(id+"F0.wireOp",EDGE,"E0");var subQ2=makeQuery(id+"F0.imprint","INTERSECT",VERTEX,{"derivedFrom":[subQ1,subQ0]});Q1=makeQuery(id+"F0.imprint","IMPRINT",FACE,{"disambiguationData":[TD([[makeQuery(id+"F0.imprint","IMPRINT",EDGE,{"disambiguationData":[TD([[subQ2,-1.0]])],"derivedFrom":subQ1}),1.0]])]});}
            var Q2;
            {var subQ0=sQuery(id+"F0.wireOp",EDGE,"E6");var subQ1=sQuery(id+"F0.wireOp",EDGE,"E0");var subQ2=makeQuery(id+"F0.imprint","INTERSECT",VERTEX,{"derivedFrom":[subQ1,subQ0]});Q2=makeQuery(id+"F0.imprint","IMPRINT",FACE,{"disambiguationData":[TD([[makeQuery(id+"F0.imprint","IMPRINT",EDGE,{"disambiguationData":[TD([[subQ2,-1.0]])],"derivedFrom":subQ1}),1.0]])]});}
            var Q3;
            {var subQ0=sQuery(id+"F0.wireOp",EDGE,"E22");var subQ1=sQuery(id+"F0.wireOp",EDGE,"E0");var subQ2=makeQuery(id+"F0.imprint","INTERSECT",VERTEX,{"derivedFrom":[subQ1,subQ0]});Q3=makeQuery(id+"F0.imprint","IMPRINT",FACE,{"disambiguationData":[TD([[makeQuery(id+"F0.imprint","IMPRINT",EDGE,{"disambiguationData":[TD([[subQ2,-1.0]])],"derivedFrom":subQ1}),1.0]])]});}
            var Q4;
            {var subQ0=sQuery(id+"F0.wireOp",EDGE,"E11");var subQ1=sQuery(id+"F0.wireOp",EDGE,"E0");var subQ2=makeQuery(id+"F0.imprint","INTERSECT",VERTEX,{"derivedFrom":[subQ1,subQ0]});Q4=makeQuery(id+"F0.imprint","IMPRINT",FACE,{"disambiguationData":[TD([[makeQuery(id+"F0.imprint","IMPRINT",EDGE,{"disambiguationData":[TD([[subQ2,-1.0]])],"derivedFrom":subQ1}),1.0]])]});}
            var Q5;
            {var subQ0=sQuery(id+"F0.wireOp",EDGE,"E19");var subQ1=sQuery(id+"F0.wireOp",EDGE,"E0");var subQ2=makeQuery(id+"F0.imprint","INTERSECT",VERTEX,{"derivedFrom":[subQ1,subQ0]});Q5=makeQuery(id+"F0.imprint","IMPRINT",FACE,{"disambiguationData":[TD([[makeQuery(id+"F0.imprint","IMPRINT",EDGE,{"disambiguationData":[TD([[subQ2,-1.0]])],"derivedFrom":subQ1}),1.0]])]});}
            var Q6;
            {var subQ0=sQuery(id+"F0.wireOp",EDGE,"E7");var subQ1=sQuery(id+"F0.wireOp",EDGE,"E0");var subQ2=makeQuery(id+"F0.imprint","INTERSECT",VERTEX,{"derivedFrom":[subQ1,subQ0]});Q6=makeQuery(id+"F0.imprint","IMPRINT",FACE,{"disambiguationData":[TD([[makeQuery(id+"F0.imprint","IMPRINT",EDGE,{"disambiguationData":[TD([[subQ2,-1.0]])],"derivedFrom":subQ1}),1.0]])]});}
            var Q7;
            {var subQ0=sQuery(id+"F0.wireOp",EDGE,"E10");var subQ1=sQuery(id+"F0.wireOp",EDGE,"E0");var subQ2=makeQuery(id+"F0.imprint","INTERSECT",VERTEX,{"derivedFrom":[subQ1,subQ0]});Q7=makeQuery(id+"F0.imprint","IMPRINT",FACE,{"disambiguationData":[TD([[makeQuery(id+"F0.imprint","IMPRINT",EDGE,{"disambiguationData":[TD([[subQ2,1.0]])],"derivedFrom":subQ1}),1.0]])]});}
            var Q8;
            {var subQ0=sQuery(id+"F0.wireOp",EDGE,"E17");var subQ1=sQuery(id+"F0.wireOp",EDGE,"E0");var subQ2=makeQuery(id+"F0.imprint","INTERSECT",VERTEX,{"derivedFrom":[subQ1,subQ0]});Q8=makeQuery(id+"F0.imprint","IMPRINT",FACE,{"disambiguationData":[TD([[makeQuery(id+"F0.imprint","IMPRINT",EDGE,{"disambiguationData":[TD([[subQ2,1.0]])],"derivedFrom":subQ1}),1.0]])]});}
            var Q9;
            {var subQ0=sQuery(id+"F0.wireOp",EDGE,"E17");var subQ1=sQuery(id+"F0.wireOp",EDGE,"E0");var subQ2=makeQuery(id+"F0.imprint","INTERSECT",VERTEX,{"derivedFrom":[subQ1,subQ0]});Q9=makeQuery(id+"F0.imprint","IMPRINT",FACE,{"disambiguationData":[TD([[makeQuery(id+"F0.imprint","IMPRINT",EDGE,{"disambiguationData":[TD([[subQ2,-1.0]])],"derivedFrom":subQ1}),1.0]])]});}
            var Q10;
            {var subQ0=sQuery(id+"F0.wireOp",EDGE,"E8");var subQ1=sQuery(id+"F0.wireOp",EDGE,"E0");var subQ2=makeQuery(id+"F0.imprint","INTERSECT",VERTEX,{"derivedFrom":[subQ1,subQ0]});Q10=makeQuery(id+"F0.imprint","IMPRINT",FACE,{"disambiguationData":[TD([[makeQuery(id+"F0.imprint","IMPRINT",EDGE,{"disambiguationData":[TD([[subQ2,-1.0]])],"derivedFrom":subQ1}),1.0]])]});}
            var Q11;
            {var subQ0=sQuery(id+"F0.wireOp",EDGE,"E18");var subQ1=sQuery(id+"F0.wireOp",EDGE,"E0");var subQ2=makeQuery(id+"F0.imprint","INTERSECT",VERTEX,{"derivedFrom":[subQ1,subQ0]});Q11=makeQuery(id+"F0.imprint","IMPRINT",FACE,{"disambiguationData":[TD([[makeQuery(id+"F0.imprint","IMPRINT",EDGE,{"disambiguationData":[TD([[subQ2,-1.0]])],"derivedFrom":subQ1}),1.0]])]});}
            var Q12;
            {var subQ0=sQuery(id+"F0.wireOp",EDGE,"E14");var subQ1=sQuery(id+"F0.wireOp",EDGE,"E0");var subQ2=makeQuery(id+"F0.imprint","INTERSECT",VERTEX,{"derivedFrom":[subQ1,subQ0]});Q12=makeQuery(id+"F0.imprint","IMPRINT",FACE,{"disambiguationData":[TD([[makeQuery(id+"F0.imprint","IMPRINT",EDGE,{"disambiguationData":[TD([[subQ2,-1.0]])],"derivedFrom":subQ1}),1.0]])]});}
            var Q13;
            {var subQ0=sQuery(id+"F0.wireOp",EDGE,"E15");var subQ1=sQuery(id+"F0.wireOp",EDGE,"E0");var subQ2=makeQuery(id+"F0.imprint","INTERSECT",VERTEX,{"derivedFrom":[subQ1,subQ0]});Q13=makeQuery(id+"F0.imprint","IMPRINT",FACE,{"disambiguationData":[TD([[makeQuery(id+"F0.imprint","IMPRINT",EDGE,{"disambiguationData":[TD([[subQ2,-1.0]])],"derivedFrom":subQ1}),1.0]])]});}
            var Q14;
            {var subQ0=sQuery(id+"F0.wireOp",EDGE,"E9");var subQ1=sQuery(id+"F0.wireOp",EDGE,"E0");var subQ2=makeQuery(id+"F0.imprint","INTERSECT",VERTEX,{"derivedFrom":[subQ1,subQ0]});Q14=makeQuery(id+"F0.imprint","IMPRINT",FACE,{"disambiguationData":[TD([[makeQuery(id+"F0.imprint","IMPRINT",EDGE,{"disambiguationData":[TD([[subQ2,-1.0]])],"derivedFrom":subQ1}),1.0]])]});}
            var Q15;
            {var subQ0=sQuery(id+"F0.wireOp",EDGE,"E16");var subQ1=sQuery(id+"F0.wireOp",EDGE,"E0");var subQ2=makeQuery(id+"F0.imprint","INTERSECT",VERTEX,{"derivedFrom":[subQ1,subQ0]});Q15=makeQuery(id+"F0.imprint","IMPRINT",FACE,{"disambiguationData":[TD([[makeQuery(id+"F0.imprint","IMPRINT",EDGE,{"disambiguationData":[TD([[subQ2,-1.0]])],"derivedFrom":subQ1}),1.0]])]});}
            var Q16;
            {var subQ0=sQuery(id+"F0.wireOp",EDGE,"E13");var subQ1=sQuery(id+"F0.wireOp",EDGE,"E0");var subQ2=makeQuery(id+"F0.imprint","INTERSECT",VERTEX,{"derivedFrom":[subQ1,subQ0]});Q16=makeQuery(id+"F0.imprint","IMPRINT",FACE,{"disambiguationData":[TD([[makeQuery(id+"F0.imprint","IMPRINT",EDGE,{"disambiguationData":[TD([[subQ2,-1.0]])],"derivedFrom":subQ1}),1.0]])]});}
            var Q17;
            {var subQ0=sQuery(id+"F0.wireOp",EDGE,"E23");var subQ1=sQuery(id+"F0.wireOp",EDGE,"E0");var subQ2=makeQuery(id+"F0.imprint","INTERSECT",VERTEX,{"derivedFrom":[subQ1,subQ0]});Q17=makeQuery(id+"F0.imprint","IMPRINT",FACE,{"disambiguationData":[TD([[makeQuery(id+"F0.imprint","IMPRINT",EDGE,{"disambiguationData":[TD([[subQ2,-1.0]])],"derivedFrom":subQ1}),1.0]])]});}
            var Q18;
            {var subQ0=sQuery(id+"F0.wireOp",EDGE,"E24");var subQ1=sQuery(id+"F0.wireOp",EDGE,"E0");var subQ2=makeQuery(id+"F0.imprint","INTERSECT",VERTEX,{"derivedFrom":[subQ1,subQ0]});Q18=makeQuery(id+"F0.imprint","IMPRINT",FACE,{"disambiguationData":[TD([[makeQuery(id+"F0.imprint","IMPRINT",EDGE,{"disambiguationData":[TD([[subQ2,-1.0]])],"derivedFrom":subQ1}),1.0]])]});}
            var Q19;
            {var subQ0=sQuery(id+"F0.wireOp",EDGE,"E5");var subQ1=sQuery(id+"F0.wireOp",EDGE,"E0");var subQ2=makeQuery(id+"F0.imprint","INTERSECT",VERTEX,{"derivedFrom":[subQ1,subQ0]});Q19=makeQuery(id+"F0.imprint","IMPRINT",FACE,{"disambiguationData":[TD([[makeQuery(id+"F0.imprint","IMPRINT",EDGE,{"disambiguationData":[TD([[subQ2,-1.0]])],"derivedFrom":subQ1}),1.0]])]});}
            var Q20;
            {var subQ0=sQuery(id+"F0.wireOp",EDGE,"E12");var subQ1=sQuery(id+"F0.wireOp",EDGE,"E0");var subQ2=makeQuery(id+"F0.imprint","INTERSECT",VERTEX,{"derivedFrom":[subQ1,subQ0]});Q20=makeQuery(id+"F0.imprint","IMPRINT",FACE,{"disambiguationData":[TD([[makeQuery(id+"F0.imprint","IMPRINT",EDGE,{"disambiguationData":[TD([[subQ2,-1.0]])],"derivedFrom":subQ1}),1.0]])]});}
            extrude(context, id + "F5", {"entities" : qUnion([Q0, Q1, Q2, Q3, Q4, Q5, Q6, Q7, Q8, Q9, Q10, Q11, Q12, Q13, Q14, Q15, Q16, Q17, Q18, Q19, Q20]), "operationType" : NewBodyOperationType.ADD, "depth" : 12 * mm, "offsetDistance" : 25 * mm, "hasSecondDirection" : true, "secondDirectionOppositeDirection" : false, "secondDirectionDepth" : 1 * mm});
        }
        {
            var Q0;
            Q0=makeQuery(id+"F2.opExtrude","CAP_FACE",FACE,{"disambiguationData":[OSD([sQuery(id+"F0.wireOp",EDGE,"E15"),sQuery(id+"F0.wireOp",EDGE,"E16"),sQuery(id+"F0.wireOp",EDGE,"E17"),sQuery(id+"F0.wireOp",EDGE,"E18"),sQuery(id+"F0.wireOp",EDGE,"E19"),sQuery(id+"F0.wireOp",EDGE,"E20"),sQuery(id+"F0.wireOp",EDGE,"E21"),sQuery(id+"F0.wireOp",EDGE,"E22"),sQuery(id+"F0.wireOp",EDGE,"E23"),sQuery(id+"F0.wireOp",EDGE,"E24")])],"isStart":true});
            fillet(context, id + "F6", {"entities" : qUnion([Q0]), "radius" : 1 * mm, "tangentPropagation" : true, "rho" : .1, "crossSection" : FilletCrossSection.CONIC, "allowEdgeOverflow" : false});
        }
        {
            var Q0;
            {var subQ0=sQuery(id+"F0.wireOp",EDGE,"E3");var subQ1=makeQuery(id+"F0.imprint","INTERSECT",VERTEX,{"derivedFrom":[subQ0,sQuery(id+"F0.wireOp",EDGE,"E11")]});var subQ2=makeQuery(id+"F0.imprint","INTERSECT",VERTEX,{"derivedFrom":[subQ0,sQuery(id+"F0.wireOp",EDGE,"E20")]});var subQ3=makeQuery(id+"F0.imprint","INTERSECT",VERTEX,{"derivedFrom":[subQ0,sQuery(id+"F0.wireOp",EDGE,"E21")]});var subQ4=makeQuery(id+"F0.imprint","INTERSECT",VERTEX,{"derivedFrom":[subQ0,sQuery(id+"F0.wireOp",EDGE,"E12")]});var subQ5=makeQuery(id+"F0.imprint","INTERSECT",VERTEX,{"derivedFrom":[subQ0,sQuery(id+"F0.wireOp",EDGE,"E22")]});var subQ6=makeQuery(id+"F0.imprint","INTERSECT",VERTEX,{"derivedFrom":[subQ0,sQuery(id+"F0.wireOp",EDGE,"E23")]});var subQ7=makeQuery(id+"F0.imprint","INTERSECT",VERTEX,{"derivedFrom":[subQ0,sQuery(id+"F0.wireOp",EDGE,"E13")]});var subQ8=makeQuery(id+"F0.imprint","INTERSECT",VERTEX,{"derivedFrom":[subQ0,sQuery(id+"F0.wireOp",EDGE,"E24")]});var subQ9=makeQuery(id+"F0.imprint","INTERSECT",VERTEX,{"derivedFrom":[subQ0,sQuery(id+"F0.wireOp",EDGE,"E15")]});var subQ10=makeQuery(id+"F0.imprint","INTERSECT",VERTEX,{"derivedFrom":[subQ0,sQuery(id+"F0.wireOp",EDGE,"E14")]});var subQ11=makeQuery(id+"F0.imprint","INTERSECT",VERTEX,{"derivedFrom":[subQ0,sQuery(id+"F0.wireOp",EDGE,"E16")]});var subQ12=makeQuery(id+"F0.imprint","INTERSECT",VERTEX,{"derivedFrom":[subQ0,sQuery(id+"F0.wireOp",EDGE,"E17")]});var subQ13=makeQuery(id+"F0.imprint","INTERSECT",VERTEX,{"derivedFrom":[subQ0,sQuery(id+"F0.wireOp",EDGE,"E10")]});var subQ15=makeQuery(id+"F0.imprint","INTERSECT",VERTEX,{"derivedFrom":[subQ0,sQuery(id+"F0.wireOp",EDGE,"E18")]});Q0=makeQuery(id+"F4.boolean.opBoolean","MERGE",EDGE,{"derivedFrom":[makeQuery(id+"F3.opExtrude","CAP_EDGE",EDGE,{"disambiguationData":[OSD([subQ0]),TDD([makeQuery(id+"F0.imprint","IMPRINT",EDGE,{"disambiguationData":[TD([[subQ15,-1.0]])],"derivedFrom":subQ0})])],"isStart":false}),makeQuery(id+"F3.opExtrude","CAP_EDGE",EDGE,{"disambiguationData":[OSD([subQ0]),TDD([makeQuery(id+"F0.imprint","IMPRINT",EDGE,{"disambiguationData":[TD([[subQ11,-1.0]])],"derivedFrom":subQ0})])],"isStart":false}),makeQuery(id+"F3.opExtrude","CAP_EDGE",EDGE,{"disambiguationData":[OSD([subQ0]),TDD([makeQuery(id+"F0.imprint","IMPRINT",EDGE,{"disambiguationData":[TD([[subQ8,-1.0]])],"derivedFrom":subQ0})])],"isStart":false}),makeQuery(id+"F3.opExtrude","CAP_EDGE",EDGE,{"disambiguationData":[OSD([subQ0]),TDD([makeQuery(id+"F0.imprint","IMPRINT",EDGE,{"disambiguationData":[TD([[subQ5,-1.0]])],"derivedFrom":subQ0})])],"isStart":false}),makeQuery(id+"F3.opExtrude","CAP_EDGE",EDGE,{"disambiguationData":[OSD([subQ0]),TDD([makeQuery(id+"F0.imprint","IMPRINT",EDGE,{"disambiguationData":[TD([[subQ2,-1.0]])],"derivedFrom":subQ0})])],"isStart":false}),makeQuery(id+"F4.opExtrude","CAP_EDGE",EDGE,{"disambiguationData":[OSD([subQ0]),TDD([makeQuery(id+"F0.imprint","IMPRINT",EDGE,{"disambiguationData":[TD([[subQ15,1.0]])],"derivedFrom":subQ0}),makeQuery(id+"F0.imprint","IMPRINT",EDGE,{"disambiguationData":[TD([[subQ13,1.0]])],"derivedFrom":subQ0})])],"isStart":false}),makeQuery(id+"F4.opExtrude","CAP_EDGE",EDGE,{"disambiguationData":[OSD([subQ0]),TDD([makeQuery(id+"F0.imprint","IMPRINT",EDGE,{"disambiguationData":[TD([[subQ12,-1.0]])],"derivedFrom":subQ0}),makeQuery(id+"F0.imprint","IMPRINT",EDGE,{"disambiguationData":[TD([[subQ10,-1.0]])],"derivedFrom":subQ0})])],"isStart":false}),makeQuery(id+"F4.opExtrude","CAP_EDGE",EDGE,{"disambiguationData":[OSD([subQ0]),TDD([makeQuery(id+"F0.imprint","IMPRINT",EDGE,{"disambiguationData":[TD([[subQ9,-1.0]])],"derivedFrom":subQ0}),makeQuery(id+"F0.imprint","IMPRINT",EDGE,{"disambiguationData":[TD([[subQ7,-1.0]])],"derivedFrom":subQ0})])],"isStart":false}),makeQuery(id+"F4.opExtrude","CAP_EDGE",EDGE,{"disambiguationData":[OSD([subQ0]),TDD([makeQuery(id+"F0.imprint","IMPRINT",EDGE,{"disambiguationData":[TD([[subQ6,-1.0]])],"derivedFrom":subQ0}),makeQuery(id+"F0.imprint","IMPRINT",EDGE,{"disambiguationData":[TD([[subQ4,-1.0]])],"derivedFrom":subQ0})])],"isStart":false}),makeQuery(id+"F4.opExtrude","CAP_EDGE",EDGE,{"disambiguationData":[OSD([subQ0]),TDD([makeQuery(id+"F0.imprint","IMPRINT",EDGE,{"disambiguationData":[TD([[subQ3,-1.0]])],"derivedFrom":subQ0}),makeQuery(id+"F0.imprint","IMPRINT",EDGE,{"disambiguationData":[TD([[subQ1,-1.0]])],"derivedFrom":subQ0})])],"isStart":false})]});}
            chamfer(context, id + "F7", {"entities" : qUnion([Q0]), "width" : 0.5 * mm, "tangentPropagation" : true});
        }
        {
            var Q0;
            Q0=makeQuery(id+"F1.opExtrude","CAP_EDGE",EDGE,{"disambiguationData":[OSD([sQuery(id+"F0.wireOp",EDGE,"E2")])],"isStart":false});
            var Q1;
            Q1=makeQuery(id+"F1.opExtrude","CAP_EDGE",EDGE,{"disambiguationData":[OSD([sQuery(id+"F0.wireOp",EDGE,"E2")])],"isStart":true});
            fillet(context, id + "F8", {"entities" : qUnion([Q0, Q1]), "radius" : 1 * mm, "tangentPropagation" : true, "allowEdgeOverflow" : false});
        }
        {
            var Q0;
            Q0=makeQuery(id+"F1.opExtrude","SWEPT_BODY",BODY,{"disambiguationData":[OSD([sQuery(id+"F0.wireOp",EDGE,"E2"),sQuery(id+"F0.wireOp",EDGE,"E3"),sQuery(id+"F0.wireOp",EDGE,"E15"),sQuery(id+"F0.wireOp",EDGE,"E16"),sQuery(id+"F0.wireOp",EDGE,"E17"),sQuery(id+"F0.wireOp",EDGE,"E18"),sQuery(id+"F0.wireOp",EDGE,"E19"),sQuery(id+"F0.wireOp",EDGE,"E20"),sQuery(id+"F0.wireOp",EDGE,"E21"),sQuery(id+"F0.wireOp",EDGE,"E22"),sQuery(id+"F0.wireOp",EDGE,"E23"),sQuery(id+"F0.wireOp",EDGE,"E24")])]});
            transform(context, id + "F9", {"entities" : qUnion([Q0]), "transformType" : TransformType.TRANSLATION_3D, "dx" : 60 * mm, "dy" : 0 * mm, "dz" : 0 * mm, "makeCopy" : false});
        }
    });
